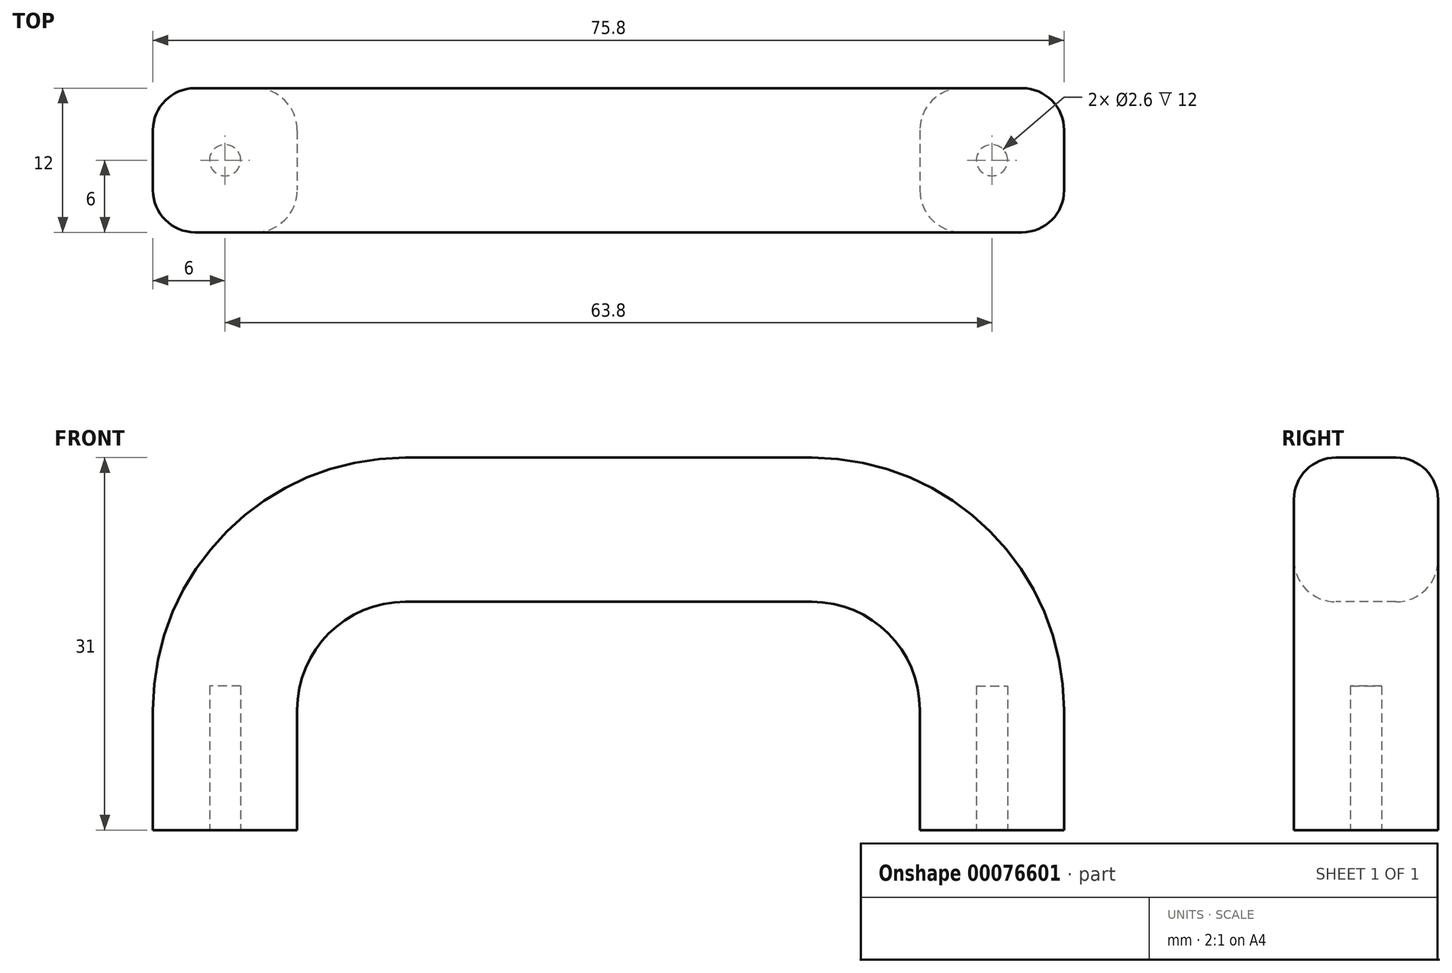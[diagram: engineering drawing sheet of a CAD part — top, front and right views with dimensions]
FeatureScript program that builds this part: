
annotation { "Feature Type Name" : "Feature", "Feature Type Description" : "" }
export const myFeature = defineFeature(function(context is Context, id is Id, definition is map)
    precondition{}
    {
        {
            var Q0;
            Q0=qCreatedBy(makeId("Top.planeOp"),FACE);
            var sketch = newSketch(context, id + "F0", { "sketchPlane" : qUnion([Q0])});
            skCircle(sketch, "E0", {"center": v(0, 0) * mm, "radius": 1.3 * mm});
            skLineSegment(sketch, "E1", {"start": v(0, 0) * mm, "end": v(31.9, 0) * mm});
            skLineSegment(sketch, "E2.bottom", {"start": v(-6, 6) * mm, "end": v(6, 6) * mm});
            skLineSegment(sketch, "E2.top", {"start": v(-6, -6) * mm, "end": v(6, -6) * mm});
            skLineSegment(sketch, "E2.left", {"start": v(-6, 6) * mm, "end": v(-6, -6) * mm});
            skLineSegment(sketch, "E2.right", {"start": v(6, 6) * mm, "end": v(6, -6) * mm});
            skLineSegment(sketch, "E3", {"start": v(0, 0) * mm, "end": v(0, 6) * mm, "construction": true});
            skLineSegment(sketch, "E4", {"start": v(0, 3) * mm, "end": v(-6, 3) * mm, "construction": true});
            skSolve(sketch);
        }
        {
            var Q0;
            Q0=qCreatedBy(makeId("Front.planeOp"),FACE);
            var Q1;
            Q1=qCreatedBy(makeId("Front.planeOp"),FACE);
            var sketch = newSketch(context, id + "F1", { "sketchPlane" : qUnion([Q0, Q1])});
            skLineSegment(sketch, "E5", {"start": v(0, 0) * mm, "end": v(0, 10) * mm});
            skLineSegment(sketch, "E6", {"start": v(15, 25) * mm, "end": v(31.9, 25) * mm});
            skPoint(sketch, "E7.visualSharp", {"position": v(0, 25) * mm});
            skArc(sketch, "E7.filletArc", {"start": v(15, 25) * mm, "mid": v(4.4, 20.6) * mm, "end": v(0, 10) * mm});
            skLineSegment(sketch, "E8", {"start": v(31.9, 25) * mm, "end": v(31.9, 0) * mm});
            skSolve(sketch);
        }
        {
            var Q0;
            Q0=makeQuery(id+"F0.imprint","IMPRINT",FACE,{"disambiguationData":[TD([[makeQuery(id+"F0.imprint","IMPRINT",EDGE,{"derivedFrom":sQuery(id+"F0.wireOp",EDGE,"E0")}),-1.0]])]});
            var Q1;
            Q1=makeQuery(id+"F0.imprint","IMPRINT",FACE,{"disambiguationData":[TD([[makeQuery(id+"F0.imprint","IMPRINT",EDGE,{"derivedFrom":sQuery(id+"F0.wireOp",EDGE,"E0")}),1.0]])]});
            var Q2;
            Q2=sQuery(id+"F1.wireOp",EDGE,"E5");
            var Q3;
            Q3=sQuery(id+"F1.wireOp",EDGE,"E7.filletArc");
            var Q4;
            Q4=sQuery(id+"F1.wireOp",EDGE,"E6");
            var Q5;
            Q5=sQuery(id+"F1.wireOp",EDGE,"55ff4bd7-6882-4591-90e0-055b6a0bfe0c.filletArc");
            var Q6;
            Q6=sQuery(id+"F1.wireOp",EDGE,"EOk1Qo79-31hJ-D282-doRE-h1Bvw1EHqyW0");
            sweep(context, id + "F2", {"profiles" : qUnion([Q0, Q1]), "path" : qUnion([Q2, Q3, Q4, Q5, Q6])});
        }
        {
            var Q0;
            Q0=makeQuery(id+"F0.imprint","IMPRINT",FACE,{"disambiguationData":[TD([[makeQuery(id+"F0.imprint","IMPRINT",EDGE,{"derivedFrom":sQuery(id+"F0.wireOp",EDGE,"E0")}),1.0]])]});
            extrude(context, id + "F3", {"entities" : qUnion([Q0]), "operationType" : NewBodyOperationType.REMOVE, "depth" : 12 * mm});
        }
        {
            var Q0;
            Q0=makeQuery(id+"F2.opSweep","SWEPT_BODY",BODY,{"disambiguationData":[OSD([sQuery(id+"F0.wireOp",EDGE,"E2.bottom"),sQuery(id+"F0.wireOp",EDGE,"E2.top"),sQuery(id+"F0.wireOp",EDGE,"E2.left"),sQuery(id+"F0.wireOp",EDGE,"E2.right"),sQuery(id+"F1.wireOp",EDGE,"E6")])]});
            var Q1;
            Q1=makeQuery(id+"F2.opSweep","CAP_FACE",FACE,{"disambiguationData":[OSD([sQuery(id+"F0.wireOp",EDGE,"E2.bottom"),sQuery(id+"F0.wireOp",EDGE,"E2.top"),sQuery(id+"F0.wireOp",EDGE,"E2.left"),sQuery(id+"F0.wireOp",EDGE,"E2.right"),sQuery(id+"F1.wireOp",VERTEX,"E6.end")])],"isStart":false});
            mirror(context, id + "F4", {"operationType" : NewBodyOperationType.ADD, "entities" : qUnion([Q0]), "mirrorPlane" : qUnion([Q1])});
        }
        {
            var Q0;
            Q0=makeQuery(id+"F2.opSweep","SWEPT_EDGE",EDGE,{"disambiguationData":[OSD([sQuery(id+"F0.wireOp",EDGE,"E2.top"),sQuery(id+"F0.wireOp",EDGE,"E2.left"),sQuery(id+"F1.wireOp",EDGE,"E7.filletArc")])]});
            var Q1;
            {var subQ0=makeQuery(id+"F2.opSweep","SWEPT_EDGE",EDGE,{"disambiguationData":[OSD([sQuery(id+"F0.wireOp",EDGE,"E2.top"),sQuery(id+"F0.wireOp",EDGE,"E2.left"),sQuery(id+"F1.wireOp",EDGE,"E6")])]});Q1=makeQuery(id+"F4.boolean.opBoolean","MERGE",EDGE,{"derivedFrom":[subQ0,makeQuery(id+"F4.opPattern","COPY",EDGE,{"derivedFrom":subQ0,"instanceName":"1"})]});}
            var Q2;
            Q2=makeQuery(id+"F4.opPattern","COPY",EDGE,{"derivedFrom":makeQuery(id+"F2.opSweep","SWEPT_EDGE",EDGE,{"disambiguationData":[OSD([sQuery(id+"F0.wireOp",EDGE,"E2.top"),sQuery(id+"F0.wireOp",EDGE,"E2.left"),sQuery(id+"F1.wireOp",EDGE,"E7.filletArc")])]}),"instanceName":"1"});
            var Q3;
            Q3=makeQuery(id+"F2.opSweep","SWEPT_EDGE",EDGE,{"disambiguationData":[OSD([sQuery(id+"F0.wireOp",EDGE,"E2.top"),sQuery(id+"F0.wireOp",EDGE,"E2.right"),sQuery(id+"F1.wireOp",EDGE,"E7.filletArc")])]});
            var Q4;
            {var subQ0=makeQuery(id+"F2.opSweep","SWEPT_EDGE",EDGE,{"disambiguationData":[OSD([sQuery(id+"F0.wireOp",EDGE,"E2.top"),sQuery(id+"F0.wireOp",EDGE,"E2.right"),sQuery(id+"F1.wireOp",EDGE,"E6")])]});Q4=makeQuery(id+"F4.boolean.opBoolean","MERGE",EDGE,{"derivedFrom":[subQ0,makeQuery(id+"F4.opPattern","COPY",EDGE,{"derivedFrom":subQ0,"instanceName":"1"})]});}
            var Q5;
            Q5=makeQuery(id+"F4.opPattern","COPY",EDGE,{"derivedFrom":makeQuery(id+"F2.opSweep","SWEPT_EDGE",EDGE,{"disambiguationData":[OSD([sQuery(id+"F0.wireOp",EDGE,"E2.top"),sQuery(id+"F0.wireOp",EDGE,"E2.right"),sQuery(id+"F1.wireOp",EDGE,"E7.filletArc")])]}),"instanceName":"1"});
            var Q6;
            Q6=makeQuery(id+"F4.opPattern","COPY",EDGE,{"derivedFrom":makeQuery(id+"F2.opSweep","SWEPT_EDGE",EDGE,{"disambiguationData":[OSD([sQuery(id+"F0.wireOp",EDGE,"E2.bottom"),sQuery(id+"F0.wireOp",EDGE,"E2.left"),sQuery(id+"F1.wireOp",EDGE,"E7.filletArc")])]}),"instanceName":"1"});
            var Q7;
            {var subQ0=makeQuery(id+"F2.opSweep","SWEPT_EDGE",EDGE,{"disambiguationData":[OSD([sQuery(id+"F0.wireOp",EDGE,"E2.bottom"),sQuery(id+"F0.wireOp",EDGE,"E2.left"),sQuery(id+"F1.wireOp",EDGE,"E6")])]});Q7=makeQuery(id+"F4.boolean.opBoolean","MERGE",EDGE,{"derivedFrom":[subQ0,makeQuery(id+"F4.opPattern","COPY",EDGE,{"derivedFrom":subQ0,"instanceName":"1"})]});}
            var Q8;
            Q8=makeQuery(id+"F4.opPattern","COPY",EDGE,{"derivedFrom":makeQuery(id+"F2.opSweep","SWEPT_EDGE",EDGE,{"disambiguationData":[OSD([sQuery(id+"F0.wireOp",EDGE,"E2.bottom"),sQuery(id+"F0.wireOp",EDGE,"E2.right"),sQuery(id+"F1.wireOp",EDGE,"E7.filletArc")])]}),"instanceName":"1"});
            var Q9;
            {var subQ0=makeQuery(id+"F2.opSweep","SWEPT_EDGE",EDGE,{"disambiguationData":[OSD([sQuery(id+"F0.wireOp",EDGE,"E2.bottom"),sQuery(id+"F0.wireOp",EDGE,"E2.right"),sQuery(id+"F1.wireOp",EDGE,"E6")])]});Q9=makeQuery(id+"F4.boolean.opBoolean","MERGE",EDGE,{"derivedFrom":[subQ0,makeQuery(id+"F4.opPattern","COPY",EDGE,{"derivedFrom":subQ0,"instanceName":"1"})]});}
            var Q10;
            Q10=makeQuery(id+"F2.opSweep","SWEPT_EDGE",EDGE,{"disambiguationData":[OSD([sQuery(id+"F0.wireOp",EDGE,"E2.bottom"),sQuery(id+"F0.wireOp",EDGE,"E2.right"),sQuery(id+"F1.wireOp",EDGE,"E7.filletArc")])]});
            var Q11;
            Q11=makeQuery(id+"F2.opSweep","SWEPT_EDGE",EDGE,{"disambiguationData":[OSD([sQuery(id+"F0.wireOp",EDGE,"E2.bottom"),sQuery(id+"F0.wireOp",EDGE,"E2.right"),sQuery(id+"F1.wireOp",EDGE,"E5")])]});
            var Q12;
            Q12=makeQuery(id+"F4.opPattern","COPY",EDGE,{"derivedFrom":makeQuery(id+"F2.opSweep","SWEPT_EDGE",EDGE,{"disambiguationData":[OSD([sQuery(id+"F0.wireOp",EDGE,"E2.bottom"),sQuery(id+"F0.wireOp",EDGE,"E2.right"),sQuery(id+"F1.wireOp",EDGE,"E5")])]}),"instanceName":"1"});
            var Q13;
            Q13=makeQuery(id+"F4.opPattern","COPY",EDGE,{"derivedFrom":makeQuery(id+"F2.opSweep","SWEPT_EDGE",EDGE,{"disambiguationData":[OSD([sQuery(id+"F0.wireOp",EDGE,"E2.bottom"),sQuery(id+"F0.wireOp",EDGE,"E2.left"),sQuery(id+"F1.wireOp",EDGE,"E5")])]}),"instanceName":"1"});
            var Q14;
            Q14=makeQuery(id+"F4.opPattern","COPY",EDGE,{"derivedFrom":makeQuery(id+"F2.opSweep","SWEPT_EDGE",EDGE,{"disambiguationData":[OSD([sQuery(id+"F0.wireOp",EDGE,"E2.top"),sQuery(id+"F0.wireOp",EDGE,"E2.left"),sQuery(id+"F1.wireOp",EDGE,"E5")])]}),"instanceName":"1"});
            var Q15;
            Q15=makeQuery(id+"F4.opPattern","COPY",EDGE,{"derivedFrom":makeQuery(id+"F2.opSweep","SWEPT_EDGE",EDGE,{"disambiguationData":[OSD([sQuery(id+"F0.wireOp",EDGE,"E2.top"),sQuery(id+"F0.wireOp",EDGE,"E2.right"),sQuery(id+"F1.wireOp",EDGE,"E5")])]}),"instanceName":"1"});
            var Q16;
            Q16=makeQuery(id+"F2.opSweep","SWEPT_EDGE",EDGE,{"disambiguationData":[OSD([sQuery(id+"F0.wireOp",EDGE,"E2.top"),sQuery(id+"F0.wireOp",EDGE,"E2.right"),sQuery(id+"F1.wireOp",EDGE,"E5")])]});
            var Q17;
            Q17=makeQuery(id+"F2.opSweep","SWEPT_EDGE",EDGE,{"disambiguationData":[OSD([sQuery(id+"F0.wireOp",EDGE,"E2.top"),sQuery(id+"F0.wireOp",EDGE,"E2.left"),sQuery(id+"F1.wireOp",EDGE,"E5")])]});
            var Q18;
            Q18=makeQuery(id+"F2.opSweep","SWEPT_EDGE",EDGE,{"disambiguationData":[OSD([sQuery(id+"F0.wireOp",EDGE,"E2.bottom"),sQuery(id+"F0.wireOp",EDGE,"E2.left"),sQuery(id+"F1.wireOp",EDGE,"E7.filletArc")])]});
            var Q19;
            Q19=makeQuery(id+"F2.opSweep","SWEPT_EDGE",EDGE,{"disambiguationData":[OSD([sQuery(id+"F0.wireOp",EDGE,"E2.bottom"),sQuery(id+"F0.wireOp",EDGE,"E2.left"),sQuery(id+"F1.wireOp",EDGE,"E5")])]});
            fillet(context, id + "F5", {"entities" : qUnion([Q0, Q1, Q2, Q3, Q4, Q5, Q6, Q7, Q8, Q9, Q10, Q11, Q12, Q13, Q14, Q15, Q16, Q17, Q18, Q19]), "radius" : 3.5 * mm, "tangentPropagation" : true, "allowEdgeOverflow" : false});
        }
    });
